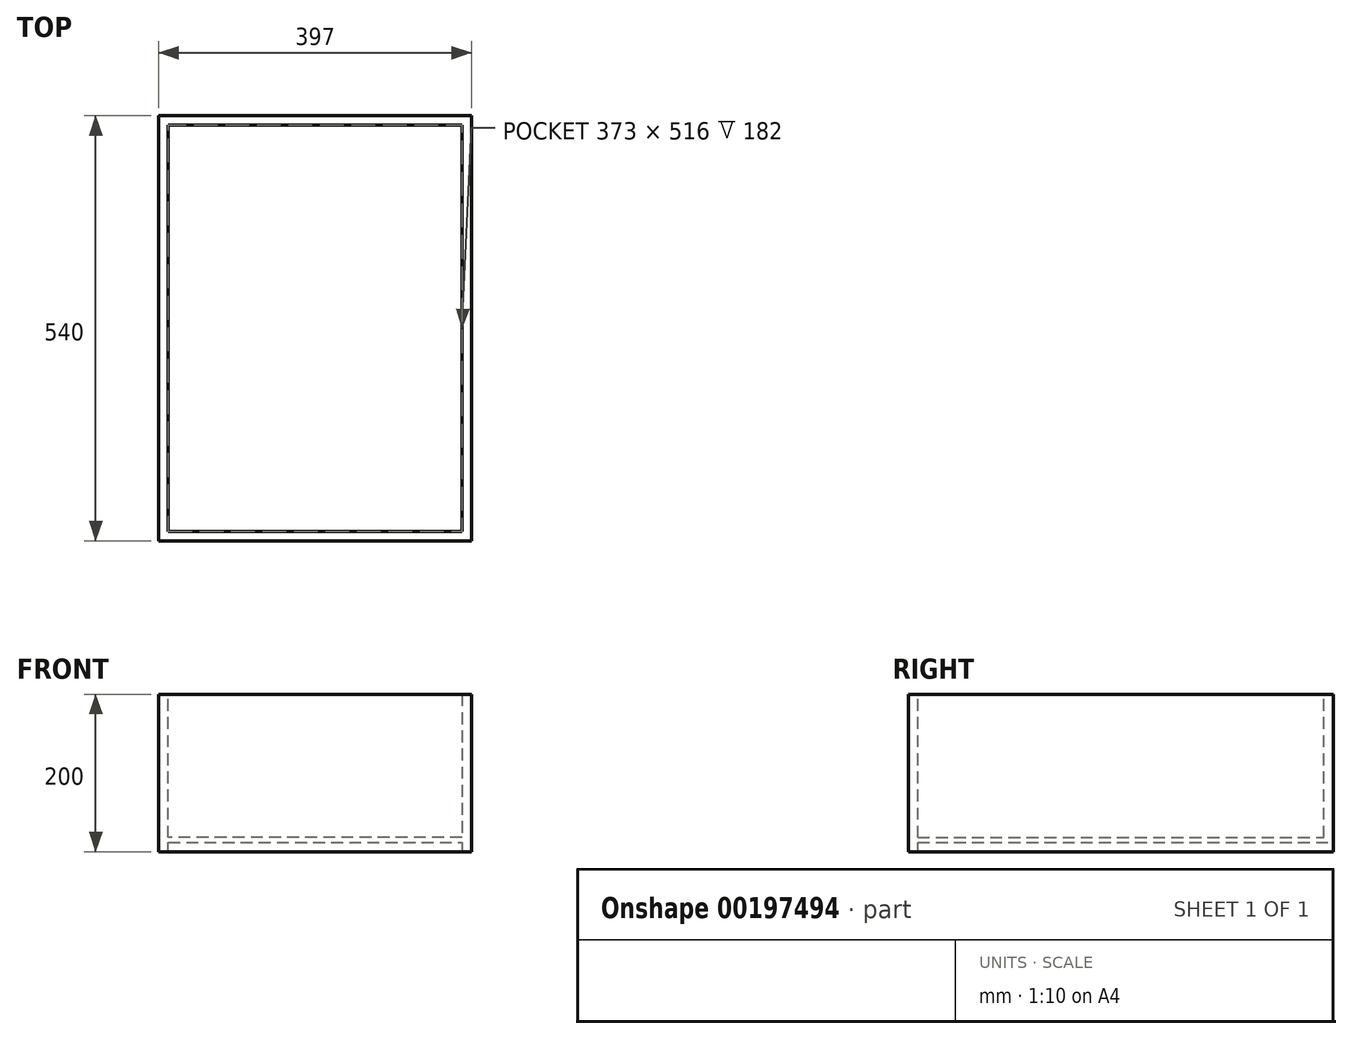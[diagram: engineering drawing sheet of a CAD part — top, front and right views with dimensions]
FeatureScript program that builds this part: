
annotation { "Feature Type Name" : "Feature", "Feature Type Description" : "" }
export const myFeature = defineFeature(function(context is Context, id is Id, definition is map)
    precondition{}
    {
        {
            var Q0;
            Q0=qCreatedBy(makeId("Front.planeOp"),FACE);
            var sketch = newSketch(context, id + "F0", { "sketchPlane" : qUnion([Q0])});
            skLineSegment(sketch, "E0", {"start": v(0, 0) * mm, "end": v(-186, 0) * mm});
            skLineSegment(sketch, "E1", {"start": v(-186, 0) * mm, "end": v(-186, 182) * mm});
            skLineSegment(sketch, "E2", {"start": v(-186, 182) * mm, "end": v(-198, 182) * mm});
            skLineSegment(sketch, "E3", {"start": v(-198, 182) * mm, "end": v(-198, -18) * mm});
            skLineSegment(sketch, "E4", {"start": v(-198, -18) * mm, "end": v(-186, -18) * mm});
            skLineSegment(sketch, "E5", {"start": v(-186, -18) * mm, "end": v(-186, -6) * mm});
            skLineSegment(sketch, "E6", {"start": v(-186, -6) * mm, "end": v(187, -6) * mm});
            skLineSegment(sketch, "E7", {"start": v(187, -6) * mm, "end": v(187, -18) * mm});
            skLineSegment(sketch, "E8", {"start": v(187, -18) * mm, "end": v(199, -18) * mm});
            skLineSegment(sketch, "E9", {"start": v(199, -18) * mm, "end": v(199, 182) * mm});
            skLineSegment(sketch, "E10", {"start": v(199, 182) * mm, "end": v(187, 182) * mm});
            skLineSegment(sketch, "E11", {"start": v(187, 182) * mm, "end": v(187, 0) * mm});
            skLineSegment(sketch, "E12", {"start": v(187, 0) * mm, "end": v(0, 0) * mm});
            skSolve(sketch);
        }
        {
            var Q0;
            Q0 = qSketchRegion(id + "F0", true);
            extrude(context, id + "F1", {"entities" : qUnion([Q0]), "depth" : 540 * mm});
        }
        {
            var Q0;
            Q0=makeQuery(id+"F1.opExtrude","SWEPT_FACE",FACE,{"disambiguationData":[OSD([sQuery(id+"F0.wireOp",EDGE,"E1")])]});
            var sketch = newSketch(context, id + "F2", { "sketchPlane" : qUnion([Q0])});
            skLineSegment(sketch, "E13.bottom", {"start": v(0, 0) * mm, "end": v(-12, 0) * mm});
            skLineSegment(sketch, "E13.top", {"start": v(0, 182) * mm, "end": v(-12, 182) * mm});
            skLineSegment(sketch, "E13.left", {"start": v(0, 0) * mm, "end": v(0, 182) * mm});
            skLineSegment(sketch, "E13.right", {"start": v(-12, 0) * mm, "end": v(-12, 182) * mm});
            skLineSegment(sketch, "E14.bottom", {"start": v(-540, -18) * mm, "end": v(-528, -18) * mm});
            skLineSegment(sketch, "E14.top", {"start": v(-540, 182) * mm, "end": v(-528, 182) * mm});
            skLineSegment(sketch, "E14.left", {"start": v(-540, -18) * mm, "end": v(-540, 182) * mm});
            skLineSegment(sketch, "E14.right", {"start": v(-528, -18) * mm, "end": v(-528, 182) * mm});
            skSolve(sketch);
        }
        {
            var Q0;
            {var subQ0=sQuery(id+"F2.wireOp",EDGE,"E14.top");Q0=makeQuery(id+"F2.imprint","IMPRINT",FACE,{"disambiguationData":[TD([[makeQuery(id+"F2.imprint","IMPRINT",EDGE,{"derivedFrom":subQ0}),-1.0]])]});}
            var Q1;
            {var subQ0=sQuery(id+"F2.wireOp",EDGE,"E14.bottom");Q1=makeQuery(id+"F2.imprint","IMPRINT",FACE,{"disambiguationData":[TD([[makeQuery(id+"F2.imprint","IMPRINT",EDGE,{"derivedFrom":subQ0}),1.0]])]});}
            var Q2;
            Q2=makeQuery(id+"F2.imprint","IMPRINT",FACE,{"disambiguationData":[TD([[makeQuery(id+"F2.imprint","IMPRINT",EDGE,{"derivedFrom":sQuery(id+"F2.wireOp",EDGE,"E13.bottom")}),1.0]])]});
            extrude(context, id + "F3", {"entities" : qUnion([Q0, Q1, Q2]), "operationType" : NewBodyOperationType.ADD, "depth" : 380 * mm});
        }
    });
